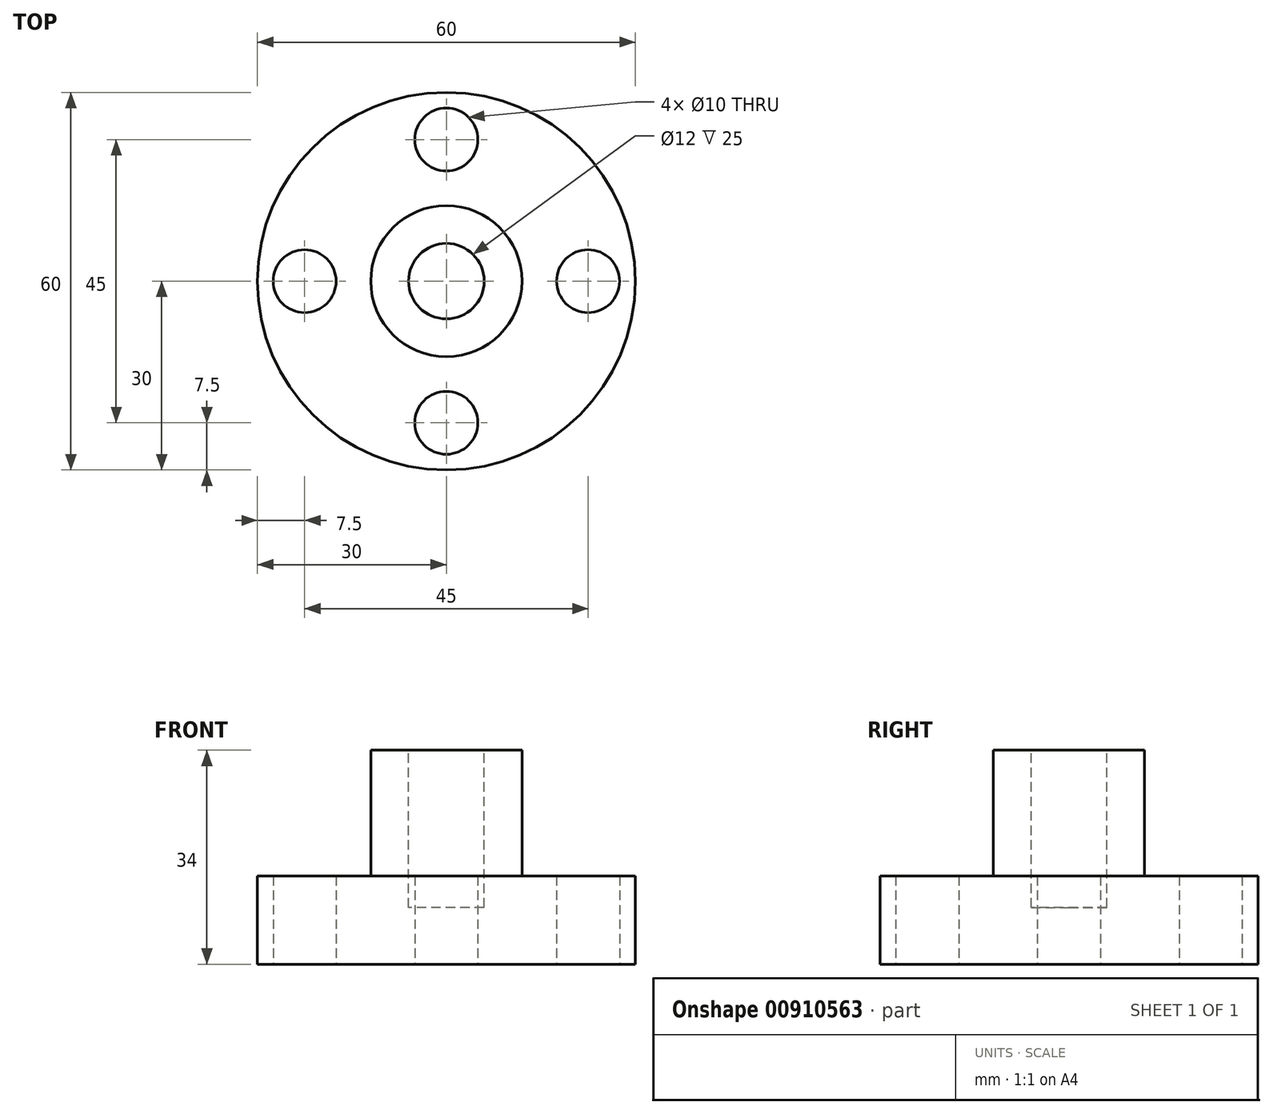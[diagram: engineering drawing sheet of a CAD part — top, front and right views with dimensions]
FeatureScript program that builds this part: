
annotation { "Feature Type Name" : "Feature", "Feature Type Description" : "" }
export const myFeature = defineFeature(function(context is Context, id is Id, definition is map)
    precondition{}
    {
        {
            var Q0;
            Q0=qCreatedBy(makeId("Top.planeOp"),FACE);
            var sketch = newSketch(context, id + "F0", { "sketchPlane" : qUnion([Q0])});
            skCircle(sketch, "E0", {"center": v(0, 0) * mm, "radius": 30 * mm});
            skSolve(sketch);
        }
        {
            var Q0;
            Q0=makeQuery(id+"F0.imprint","IMPRINT",FACE,{"disambiguationData":[TD([[makeQuery(id+"F0.imprint","IMPRINT",EDGE,{"derivedFrom":sQuery(id+"F0.wireOp",EDGE,"E0")}),1.0]])]});
            extrude(context, id + "F1", {"entities" : qUnion([Q0]), "depth" : 14 * mm, "offsetDistance" : 25 * mm});
        }
        {
            var Q0;
            Q0=makeQuery(id+"F1.opExtrude","CAP_FACE",FACE,{"disambiguationData":[OSD([sQuery(id+"F0.wireOp",EDGE,"E0")])],"isStart":false});
            var sketch = newSketch(context, id + "F2", { "sketchPlane" : qUnion([Q0])});
            skCircle(sketch, "E1", {"center": v(0, 0) * mm, "radius": 12 * mm});
            skSolve(sketch);
        }
        {
            var Q0;
            Q0=makeQuery(id+"F2.imprint","IMPRINT",FACE,{"disambiguationData":[TD([[makeQuery(id+"F2.imprint","IMPRINT",EDGE,{"derivedFrom":sQuery(id+"F2.wireOp",EDGE,"E1")}),1.0]])]});
            extrude(context, id + "F3", {"entities" : qUnion([Q0]), "operationType" : NewBodyOperationType.ADD, "depth" : 20 * mm, "offsetDistance" : 25 * mm});
        }
        {
            var Q0;
            Q0=makeQuery(id+"F3.opExtrude","CAP_FACE",FACE,{"disambiguationData":[OSD([sQuery(id+"F2.wireOp",EDGE,"E1")])],"isStart":false});
            var sketch = newSketch(context, id + "F4", { "sketchPlane" : qUnion([Q0])});
            skCircle(sketch, "E2", {"center": v(0, 0) * mm, "radius": 6 * mm});
            skSolve(sketch);
        }
        {
            var Q0;
            Q0=makeQuery(id+"F4.imprint","IMPRINT",FACE,{"disambiguationData":[TD([[makeQuery(id+"F4.imprint","IMPRINT",EDGE,{"derivedFrom":sQuery(id+"F4.wireOp",EDGE,"E2")}),1.0]])]});
            extrude(context, id + "F5", {"entities" : qUnion([Q0]), "operationType" : NewBodyOperationType.REMOVE, "oppositeDirection" : true, "depth" : 25 * mm, "offsetDistance" : 25 * mm});
        }
        {
            var Q0;
            Q0=makeQuery(id+"F1.opExtrude","CAP_FACE",FACE,{"disambiguationData":[OSD([sQuery(id+"F0.wireOp",EDGE,"E0")])],"isStart":true});
            var sketch = newSketch(context, id + "F6", { "sketchPlane" : qUnion([Q0])});
            skCircle(sketch, "E3", {"center": v(0, 22.5) * mm, "radius": 5 * mm});
            skCircle(sketch, "E4", {"center": v(0, -22.5) * mm, "radius": 5 * mm});
            skCircle(sketch, "E5", {"center": v(22.5, 0) * mm, "radius": 5 * mm});
            skCircle(sketch, "E6", {"center": v(-22.5, 0) * mm, "radius": 5 * mm});
            skSolve(sketch);
        }
        {
            var Q0;
            Q0=makeQuery(id+"F6.imprint","IMPRINT",FACE,{"disambiguationData":[TD([[makeQuery(id+"F6.imprint","IMPRINT",EDGE,{"derivedFrom":sQuery(id+"F6.wireOp",EDGE,"E4")}),1.0]])]});
            extrude(context, id + "F7", {"entities" : qUnion([Q0]), "operationType" : NewBodyOperationType.REMOVE, "endBound" : BoundingType.THROUGH_ALL, "oppositeDirection" : true, "depth" : 25 * mm, "offsetDistance" : 25 * mm});
        }
        {
            var Q0;
            Q0=makeQuery(id+"F1.opExtrude","CAP_FACE",FACE,{"disambiguationData":[OSD([sQuery(id+"F0.wireOp",EDGE,"E0")])],"isStart":true});
            var sketch = newSketch(context, id + "F8", { "sketchPlane" : qUnion([Q0])});
            skCircle(sketch, "E7", {"center": v(0, 22.5) * mm, "radius": 5 * mm});
            skSolve(sketch);
        }
        {
            var Q0;
            Q0=makeQuery(id+"F8.imprint","IMPRINT",FACE,{"disambiguationData":[TD([[makeQuery(id+"F8.imprint","IMPRINT",EDGE,{"derivedFrom":sQuery(id+"F8.wireOp",EDGE,"E7")}),1.0]])]});
            extrude(context, id + "F9", {"entities" : qUnion([Q0]), "operationType" : NewBodyOperationType.REMOVE, "endBound" : BoundingType.THROUGH_ALL, "oppositeDirection" : true, "depth" : 25 * mm, "offsetDistance" : 25 * mm});
        }
        {
            var Q0;
            Q0=makeQuery(id+"F1.opExtrude","CAP_FACE",FACE,{"disambiguationData":[OSD([sQuery(id+"F0.wireOp",EDGE,"E0")])],"isStart":true});
            var sketch = newSketch(context, id + "F10", { "sketchPlane" : qUnion([Q0])});
            skCircle(sketch, "E8", {"center": v(-22.5, 0) * mm, "radius": 5 * mm});
            skSolve(sketch);
        }
        {
            var Q0;
            Q0=makeQuery(id+"F10.imprint","IMPRINT",FACE,{"disambiguationData":[TD([[makeQuery(id+"F10.imprint","IMPRINT",EDGE,{"derivedFrom":sQuery(id+"F10.wireOp",EDGE,"E8")}),1.0]])]});
            extrude(context, id + "F11", {"entities" : qUnion([Q0]), "operationType" : NewBodyOperationType.REMOVE, "endBound" : BoundingType.THROUGH_ALL, "oppositeDirection" : true, "depth" : 25 * mm, "offsetDistance" : 25 * mm});
        }
        {
            var Q0;
            Q0=makeQuery(id+"F1.opExtrude","CAP_FACE",FACE,{"disambiguationData":[OSD([sQuery(id+"F0.wireOp",EDGE,"E0")])],"isStart":true});
            var sketch = newSketch(context, id + "F12", { "sketchPlane" : qUnion([Q0])});
            skCircle(sketch, "E9", {"center": v(22.5, 0) * mm, "radius": 5 * mm});
            skSolve(sketch);
        }
        {
            var Q0;
            Q0=makeQuery(id+"F12.imprint","IMPRINT",FACE,{"disambiguationData":[TD([[makeQuery(id+"F12.imprint","IMPRINT",EDGE,{"derivedFrom":sQuery(id+"F12.wireOp",EDGE,"E9")}),1.0]])]});
            extrude(context, id + "F13", {"entities" : qUnion([Q0]), "operationType" : NewBodyOperationType.REMOVE, "endBound" : BoundingType.THROUGH_ALL, "oppositeDirection" : true, "depth" : 25 * mm, "offsetDistance" : 25 * mm});
        }
    });
